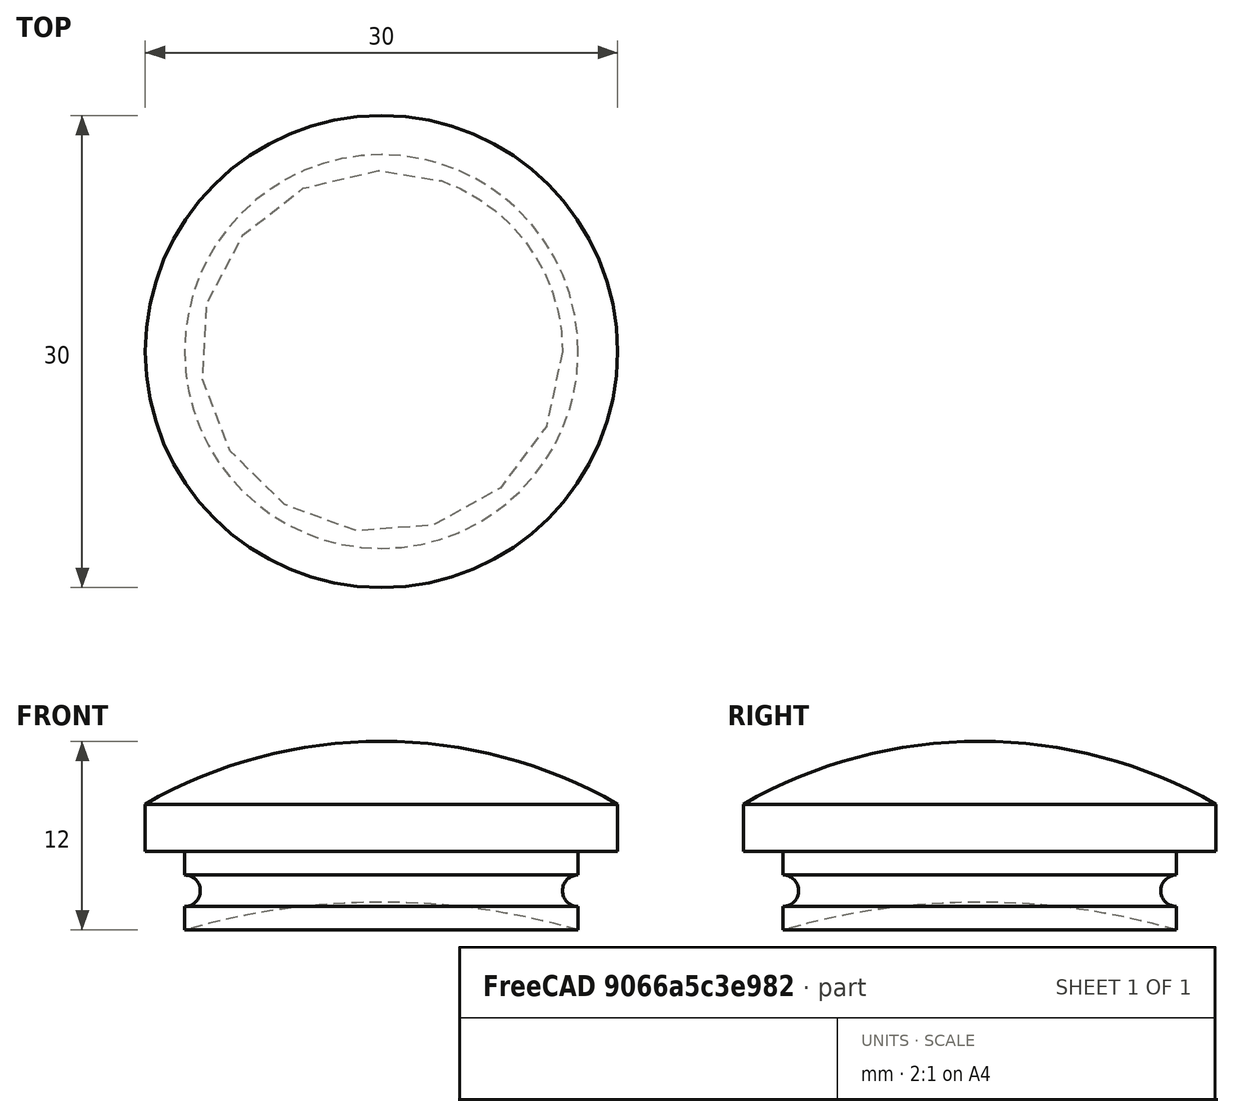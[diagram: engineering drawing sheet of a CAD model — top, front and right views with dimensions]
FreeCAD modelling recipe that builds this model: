
FCSTD DOCUMENT  (FreeCAD 0.18R16146 (Git))
Label: ObjectiveLense
License: All rights reserved
LicenseURL: http://en.wikipedia.org/wiki/All_rights_reserved
objects: Sketcher::SketchObject×1, PartDesign::Revolution×1, PartDesign::Body×1
note: 4 computed .brp shape members not serialized (recipe doc carries the construction recipe); baked Part::Feature solids carry a one-line shape summary decoded from their .brp

FEATURE [Sketcher::SketchObject] Sketch
  MapMode = 5
  Placement = pos=(0,0,0) rot=(1,0,0;1.5708rad)
  Support = -> [XZ_Plane]
  sketch-geometry (9):
    g0: LineSegment StartX=1.8e-15 StartY=12 StartZ=0 EndX=1.8e-15 EndY=1.77096 EndZ=0
    g1: ArcOfCircle CenterX=0 CenterY=-18.125 CenterZ=0 NormalX=0 NormalY=0 NormalZ=1 AngleXU=0 Radius=30.125 StartAngle=1.04959 EndAngle=1.5708
    g2: ArcOfCircle CenterX=0 CenterY=-43.229 CenterZ=0 NormalX=0 NormalY=0 NormalZ=1 AngleXU=0 Radius=45 StartAngle=1.28932 EndAngle=1.5708
    g3: LineSegment StartX=15 StartY=8 StartZ=0 EndX=15 EndY=5 EndZ=0
    g4: LineSegment StartX=15 StartY=5 StartZ=0 EndX=12.5 EndY=5 EndZ=0
    g5: LineSegment [constr] StartX=12.5 StartY=5 StartZ=0 EndX=12.5 EndY=0 EndZ=0
    g6: ArcOfCircle CenterX=12.5 CenterY=2.5 CenterZ=0 NormalX=0 NormalY=0 NormalZ=1 AngleXU=0 Radius=1 StartAngle=1.5708 EndAngle=4.71239
    g7: LineSegment StartX=12.5 StartY=5 StartZ=0 EndX=12.5 EndY=3.5 EndZ=0
    g8: LineSegment StartX=12.5 StartY=1.5 StartZ=0 EndX=12.5 EndY=1.1e-15 EndZ=0
  constraints (29):
    c: PointOnObject(g0,g-2)
    c: Vertical(g0)
    c: PointOnObject(g1,g-2)
    c: Coincident(g1,g0)
    c: PointOnObject(g2,g-2)
    c: Coincident(g0,g2)
    c: DistanceY(g2,g0) = 12
    c: DistanceX(g0,g1) = 15
    c: Coincident(g3,g1)
    c: Vertical(g3)
    c: Coincident(g4,g3)
    c: Horizontal(g4)
    c: Coincident(g4,g5)
    c: Vertical(g5)
    c: Coincident(g2,g5)
    c: DistanceX(g0,g2) = 12.5
    c: DistanceY(g2,g3) = 5
    c: DistanceY(g2,g0) = 45
    c: PointOnObject(g2,g-1)
    c: DistanceY(g3,g1) = 3
    c: PointOnObject(g6,g5)
    c: PointOnObject(g6,g5)
    c: Radius(g6) = 1
    c: Symmetric(g4,g2,g6)
    c: Coincident(g7,g6)
    c: PointOnObject(g8,g2)
    c: Vertical(g8)
    c: Coincident(g8,g6)
    c: Coincident(g7,g4)
FEATURE [PartDesign::Revolution] Revolution
  Angle = 360
  Axis = (0,-1.031e-13,1)
  Base = (0,0,0)
  Placement = pos=(0,0,0) rot=(1,0,0;1.5708rad)
  Profile = -> Sketch
  ReferenceAxis = -> Sketch [V_Axis]
  Reversed = true
FEATURE [PartDesign::Body] Body
  Group = -> [Sketch,Revolution]
  Origin = -> Origin
  Tip = -> Revolution
